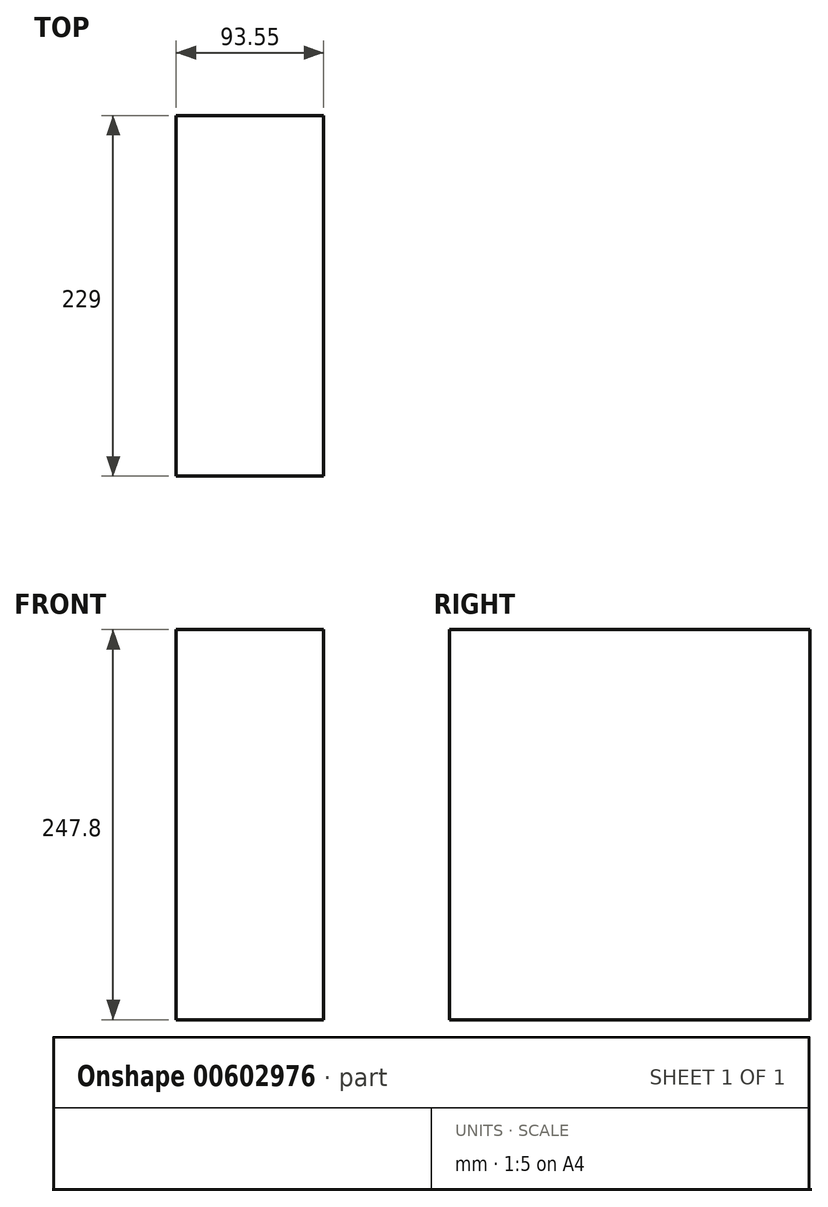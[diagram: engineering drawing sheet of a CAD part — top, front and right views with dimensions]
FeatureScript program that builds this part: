
annotation { "Feature Type Name" : "Feature", "Feature Type Description" : "" }
export const myFeature = defineFeature(function(context is Context, id is Id, definition is map)
    precondition{}
    {
        {
            var Q0;
            Q0=qCreatedBy(makeId("Right.planeOp"),FACE);
            var sketch = newSketch(context, id + "F0", { "sketchPlane" : qUnion([Q0])});
            skLineSegment(sketch, "E0.bottom", {"start": v(114.5, -123.9) * mm, "end": v(-114.5, -123.9) * mm});
            skLineSegment(sketch, "E0.top", {"start": v(114.5, 123.9) * mm, "end": v(-114.5, 123.9) * mm});
            skLineSegment(sketch, "E0.left", {"start": v(114.5, -123.9) * mm, "end": v(114.5, 123.9) * mm});
            skLineSegment(sketch, "E0.right", {"start": v(-114.5, -123.9) * mm, "end": v(-114.5, 123.9) * mm});
            skPoint(sketch, "E0.middle", {"position": v(0, 0) * mm});
            skSolve(sketch);
        }
        {
            var Q0;
            Q0=makeQuery(id+"F0.imprint","IMPRINT",FACE,{"disambiguationData":[TD([[makeQuery(id+"F0.imprint","IMPRINT",EDGE,{"derivedFrom":sQuery(id+"F0.wireOp",EDGE,"E0.bottom")}),-1.0]])]});
            var sketch = newSketch(context, id + "F1", { "sketchPlane" : qUnion([Q0])});
            skSolve(sketch);
        }
        {
            var Q0;
            Q0 = qSketchRegion(id + "F1", true);
            var Q1;
            Q1=makeQuery(id+"F1.imprint","IMPRINT",FACE,{"disambiguationData":[TD([[makeQuery(id+"F1.imprint","IMPRINT",EDGE,{"derivedFrom":makeQuery(id+"F0.imprint","IMPRINT",EDGE,{"derivedFrom":sQuery(id+"F0.wireOp",EDGE,"E0.bottom")})}),-1.0]])]});
            extrude(context, id + "F2", {"entities" : qUnion([Q0, Q1]), "depth" : 93.55 * mm, "offsetDistance" : 25.4 * mm});
        }
    });
